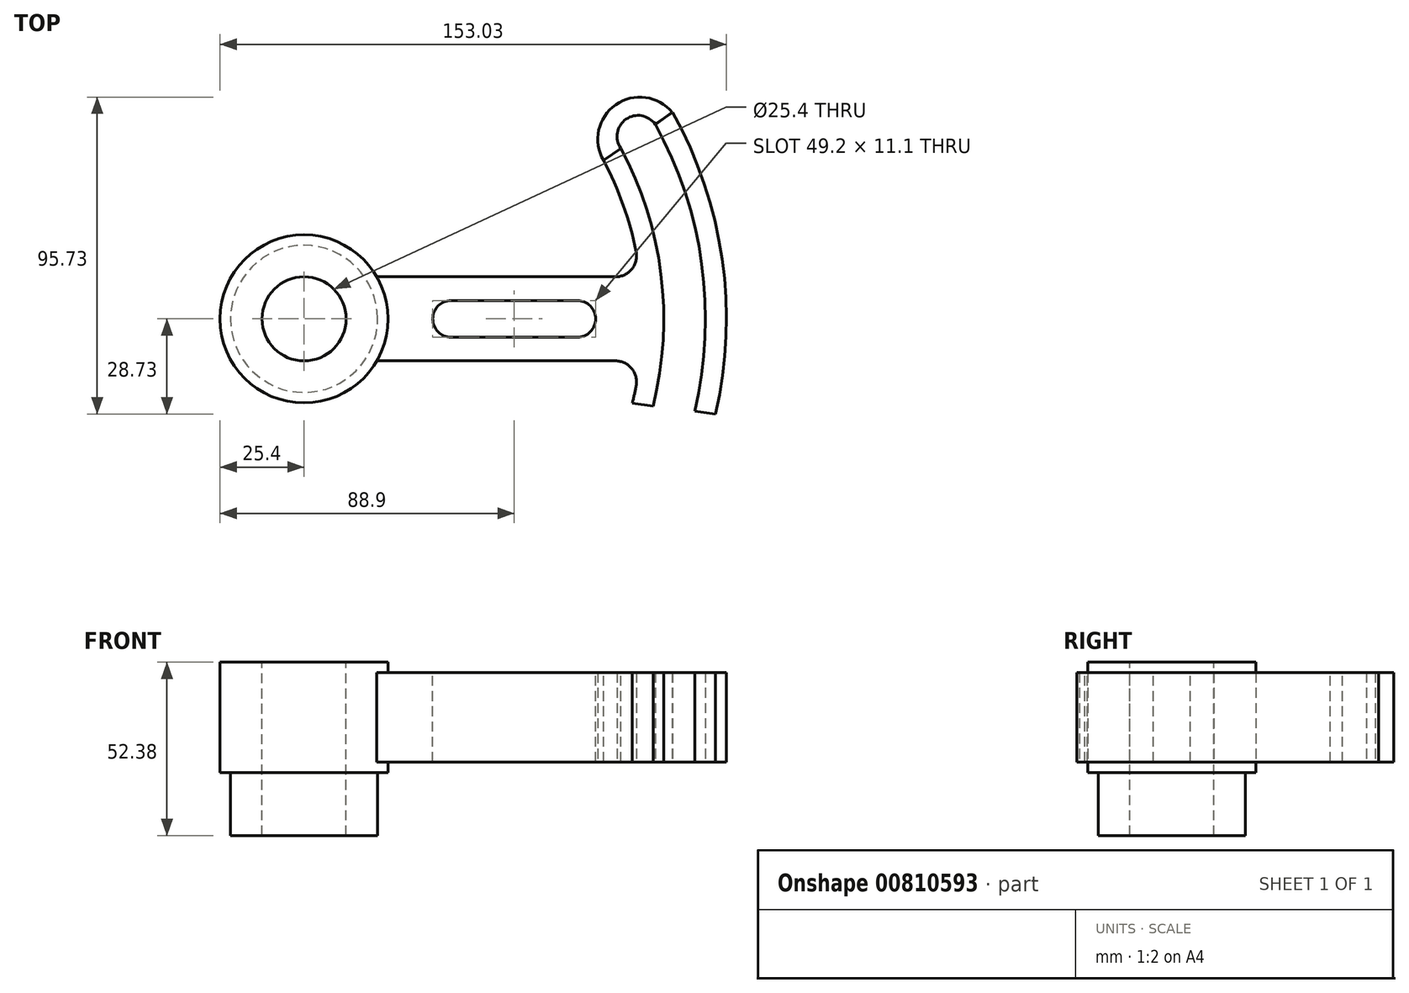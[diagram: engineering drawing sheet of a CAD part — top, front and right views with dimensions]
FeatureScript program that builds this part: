
annotation { "Feature Type Name" : "Feature", "Feature Type Description" : "" }
export const myFeature = defineFeature(function(context is Context, id is Id, definition is map)
    precondition{}
    {
        {
            var Q0;
            Q0=qCreatedBy(makeId("Top.planeOp"),FACE);
            var sketch = newSketch(context, id + "F0", { "sketchPlane" : qUnion([Q0])});
            skCircle(sketch, "E0", {"center": v(0, 0) * mm, "radius": 25.4 * mm});
            skLineSegment(sketch, "E1", {"start": v(22, 12.7) * mm, "end": v(114.45, 12.7) * mm});
            skLineSegment(sketch, "E2", {"start": v(22, -12.7) * mm, "end": v(114.45, -12.7) * mm});
            skLineSegment(sketch, "E3", {"start": v(114.45, 12.7) * mm, "end": v(114.45, -12.7) * mm});
            skSolve(sketch);
        }
        {
            var Q0;
            {var subQ0=sQuery(id+"F0.wireOp",EDGE,"E1");Q0=makeQuery(id+"F0.imprint","IMPRINT",FACE,{"disambiguationData":[TD([[makeQuery(id+"F0.imprint","IMPRINT",EDGE,{"derivedFrom":subQ0}),-1.0]])]});}
            extrude(context, id + "F1", {"entities" : qUnion([Q0]), "depth" : 26.97 * mm, "offsetDistance" : 25.4 * mm});
        }
        {
            var Q0;
            Q0=makeQuery(id+"F1.opExtrude","CAP_FACE",FACE,{"disambiguationData":[OSD([sQuery(id+"F0.wireOp",EDGE,"E0"),sQuery(id+"F0.wireOp",EDGE,"E1"),sQuery(id+"F0.wireOp",EDGE,"E2"),sQuery(id+"F0.wireOp",EDGE,"E3")])],"isStart":false});
            var sketch = newSketch(context, id + "F2", { "sketchPlane" : qUnion([Q0])});
            skLineSegment(sketch, "E4.bottom", {"start": v(44.45, 5.55) * mm, "end": v(82.55, 5.55) * mm});
            skLineSegment(sketch, "E4.top", {"start": v(44.45, -5.55) * mm, "end": v(82.55, -5.55) * mm});
            skLineSegment(sketch, "E4.left", {"start": v(44.45, 5.55) * mm, "end": v(44.45, -5.55) * mm});
            skLineSegment(sketch, "E4.right", {"start": v(82.55, 5.55) * mm, "end": v(82.55, -5.55) * mm});
            skSolve(sketch);
        }
        {
            var Q0;
            Q0=makeQuery(id+"F2.imprint","IMPRINT",FACE,{"disambiguationData":[TD([[makeQuery(id+"F2.imprint","IMPRINT",EDGE,{"derivedFrom":sQuery(id+"F2.wireOp",EDGE,"E4.bottom")}),1.0]])]});
            var sketch = newSketch(context, id + "F3", { "sketchPlane" : qUnion([Q0])});
            skCircle(sketch, "E5", {"center": v(44.45, 0) * mm, "radius": 5.55 * mm});
            skSolve(sketch);
        }
        {
            var Q0;
            Q0=makeQuery(id+"F2.imprint","IMPRINT",FACE,{"disambiguationData":[TD([[makeQuery(id+"F2.imprint","IMPRINT",EDGE,{"derivedFrom":sQuery(id+"F2.wireOp",EDGE,"E4.bottom")}),1.0]])]});
            var sketch = newSketch(context, id + "F4", { "sketchPlane" : qUnion([Q0])});
            skCircle(sketch, "E6", {"center": v(82.55, 0) * mm, "radius": 5.55 * mm});
            skSolve(sketch);
        }
        {
            var Q0;
            {var subQ1=makeQuery(id+"F2.imprint","IMPRINT",EDGE,{"derivedFrom":sQuery(id+"F2.wireOp",EDGE,"E4.right")});Q0=makeQuery(id+"F4.imprint","IMPRINT",FACE,{"disambiguationData":[TD([[makeQuery(id+"F4.imprint","IMPRINT",EDGE,{"derivedFrom":subQ1}),1.0]])]});}
            var Q1;
            Q1=makeQuery(id+"F2.imprint","IMPRINT",FACE,{"disambiguationData":[TD([[makeQuery(id+"F2.imprint","IMPRINT",EDGE,{"derivedFrom":sQuery(id+"F2.wireOp",EDGE,"E4.bottom")}),-1.0]])]});
            var Q2;
            {var subQ1=makeQuery(id+"F2.imprint","IMPRINT",EDGE,{"derivedFrom":sQuery(id+"F2.wireOp",EDGE,"E4.left")});Q2=makeQuery(id+"F3.imprint","IMPRINT",FACE,{"disambiguationData":[TD([[makeQuery(id+"F3.imprint","IMPRINT",EDGE,{"derivedFrom":subQ1}),-1.0]])]});}
            extrude(context, id + "F5", {"entities" : qUnion([Q0, Q1, Q2]), "operationType" : NewBodyOperationType.REMOVE, "oppositeDirection" : true, "depth" : 38.1 * mm, "offsetDistance" : 25.4 * mm});
        }
        {
            var Q0;
            Q0=qCreatedBy(makeId("Top.planeOp"),FACE);
            var sketch = newSketch(context, id + "F6", { "sketchPlane" : qUnion([Q0])});
            skCircle(sketch, "E7", {"center": v(0, 0) * mm, "radius": 25.4 * mm});
            skSolve(sketch);
        }
        {
            var Q0;
            Q0=makeQuery(id+"F6.imprint","IMPRINT",FACE,{"disambiguationData":[TD([[makeQuery(id+"F6.imprint","IMPRINT",EDGE,{"derivedFrom":sQuery(id+"F6.wireOp",EDGE,"E7")}),1.0]])]});
            extrude(context, id + "F7", {"entities" : qUnion([Q0]), "operationType" : NewBodyOperationType.ADD, "depth" : 30.15 * mm, "offsetDistance" : 25.4 * mm});
        }
        {
            var Q0;
            Q0=makeQuery(id+"F7.boolean.opBoolean","MERGE",FACE,{"derivedFrom":[makeQuery(id+"F1.opExtrude","CAP_FACE",FACE,{"disambiguationData":[OSD([sQuery(id+"F0.wireOp",EDGE,"E0"),sQuery(id+"F0.wireOp",EDGE,"E1"),sQuery(id+"F0.wireOp",EDGE,"E2"),sQuery(id+"F0.wireOp",EDGE,"E3")])],"isStart":true}),makeQuery(id+"F7.opExtrude","CAP_FACE",FACE,{"disambiguationData":[OSD([sQuery(id+"F6.wireOp",EDGE,"E7")])],"isStart":true})]});
            var sketch = newSketch(context, id + "F8", { "sketchPlane" : qUnion([Q0])});
            skCircle(sketch, "E8", {"center": v(0, 0) * mm, "radius": 25.4 * mm});
            skSolve(sketch);
        }
        {
            var Q0;
            Q0 = qSketchRegion(id + "F8", true);
            extrude(context, id + "F9", {"entities" : qUnion([Q0]), "operationType" : NewBodyOperationType.ADD, "depth" : 3.17 * mm, "offsetDistance" : 25.4 * mm});
        }
        {
            var Q0;
            Q0=makeQuery(id+"F9.opExtrude","CAP_FACE",FACE,{"disambiguationData":[OSD([sQuery(id+"F8.wireOp",EDGE,"E8")])],"isStart":false});
            var sketch = newSketch(context, id + "F10", { "sketchPlane" : qUnion([Q0])});
            skCircle(sketch, "E9", {"center": v(0, 0) * mm, "radius": 22.23 * mm});
            skSolve(sketch);
        }
        {
            var Q0;
            Q0=makeQuery(id+"F10.imprint","IMPRINT",FACE,{"disambiguationData":[TD([[makeQuery(id+"F10.imprint","IMPRINT",EDGE,{"derivedFrom":sQuery(id+"F10.wireOp",EDGE,"E9")}),1.0]])]});
            extrude(context, id + "F11", {"entities" : qUnion([Q0]), "operationType" : NewBodyOperationType.ADD, "depth" : 19.05 * mm, "offsetDistance" : 25.4 * mm});
        }
        {
            var Q0;
            Q0=makeQuery(id+"F7.opExtrude","CAP_FACE",FACE,{"disambiguationData":[OSD([sQuery(id+"F6.wireOp",EDGE,"E7")])],"isStart":false});
            var sketch = newSketch(context, id + "F12", { "sketchPlane" : qUnion([Q0])});
            skCircle(sketch, "E10", {"center": v(0, 0) * mm, "radius": 12.7 * mm});
            skSolve(sketch);
        }
        {
            var Q0;
            Q0=makeQuery(id+"F12.imprint","IMPRINT",FACE,{"disambiguationData":[TD([[makeQuery(id+"F12.imprint","IMPRINT",EDGE,{"derivedFrom":sQuery(id+"F12.wireOp",EDGE,"E10")}),1.0]])]});
            extrude(context, id + "F13", {"entities" : qUnion([Q0]), "operationType" : NewBodyOperationType.REMOVE, "oppositeDirection" : true, "depth" : 61.98 * mm, "offsetDistance" : 25.4 * mm});
        }
        {
            var Q0;
            Q0=makeQuery(id+"F1.opExtrude","SWEPT_FACE",FACE,{"disambiguationData":[OSD([sQuery(id+"F0.wireOp",EDGE,"E2")])]});
            var sketch = newSketch(context, id + "F14", { "sketchPlane" : qUnion([Q0])});
            skLineSegment(sketch, "E11.bottom", {"start": v(101.6, 0) * mm, "end": v(107.95, 0) * mm});
            skLineSegment(sketch, "E11.top", {"start": v(101.6, 26.97) * mm, "end": v(107.95, 26.97) * mm});
            skLineSegment(sketch, "E11.left", {"start": v(101.6, 0) * mm, "end": v(101.6, 26.97) * mm});
            skLineSegment(sketch, "E11.right", {"start": v(107.95, 0) * mm, "end": v(107.95, 26.97) * mm});
            skLineSegment(sketch, "E12.bottom", {"start": v(120.65, 26.97) * mm, "end": v(127, 26.97) * mm});
            skLineSegment(sketch, "E12.top", {"start": v(120.65, 0) * mm, "end": v(127, 0) * mm});
            skLineSegment(sketch, "E12.left", {"start": v(120.65, 26.97) * mm, "end": v(120.65, 0) * mm});
            skLineSegment(sketch, "E12.right", {"start": v(127, 26.97) * mm, "end": v(127, 0) * mm});
            skSolve(sketch);
        }
        {
            var Q0;
            Q0=qCreatedBy(makeId("Right.planeOp"),FACE);
            var sketch = newSketch(context, id + "F15", { "sketchPlane" : qUnion([Q0])});
            skLineSegment(sketch, "E13", {"start": v(0, 0) * mm, "end": v(0, 69.13) * mm});
            skSolve(sketch);
        }
        {
            var Q0;
            Q0=makeQuery(id+"F1.opExtrude","SWEPT_FACE",FACE,{"disambiguationData":[OSD([sQuery(id+"F0.wireOp",EDGE,"E3")])]});
            extrude(context, id + "F16", {"entities" : qUnion([Q0]), "operationType" : NewBodyOperationType.REMOVE, "oppositeDirection" : true, "depth" : 7.62 * mm, "offsetDistance" : 25.4 * mm});
        }
        {
            var Q0;
            Q0=makeQuery(id+"F14.imprint","IMPRINT",FACE,{"disambiguationData":[TD([[makeQuery(id+"F14.imprint","IMPRINT",EDGE,{"derivedFrom":sQuery(id+"F14.wireOp",EDGE,"E11.bottom")}),1.0]])]});
            var Q1;
            Q1=makeQuery(id+"F14.imprint","IMPRINT",FACE,{"disambiguationData":[TD([[makeQuery(id+"F14.imprint","IMPRINT",EDGE,{"derivedFrom":sQuery(id+"F14.wireOp",EDGE,"E12.bottom")}),-1.0]])]});
            var Q2;
            Q2=sQuery(id+"F15.wireOp",EDGE,"E13");
            revolve(context, id + "F17", {"operationType" : NewBodyOperationType.ADD, "surfaceOperationType" : NewSurfaceOperationType.NEW, "entities" : qUnion([Q0, Q1]), "axis" : qUnion([Q2]), "revolveType" : RevolveType.TWO_DIRECTIONS, "angle" : 35 * degree, "angleBack" : 352.7 * degree});
        }
        {
            var Q0;
            Q0=makeQuery(id+"F17.boolean.opBoolean","MERGE",FACE,{"derivedFrom":[makeQuery(id+"F7.boolean.opBoolean","MERGE",FACE,{"derivedFrom":[makeQuery(id+"F1.opExtrude","CAP_FACE",FACE,{"disambiguationData":[OSD([sQuery(id+"F0.wireOp",EDGE,"E0"),sQuery(id+"F0.wireOp",EDGE,"E1"),sQuery(id+"F0.wireOp",EDGE,"E2"),sQuery(id+"F0.wireOp",EDGE,"E3")])],"isStart":true}),makeQuery(id+"F7.opExtrude","CAP_FACE",FACE,{"disambiguationData":[OSD([sQuery(id+"F6.wireOp",EDGE,"E7")])],"isStart":true})]}),makeQuery(id+"F17.opRevolve","SWEPT_FACE",FACE,{"disambiguationData":[OSD([sQuery(id+"F14.wireOp",EDGE,"E11.bottom")])]})]});
            var sketch = newSketch(context, id + "F18", { "sketchPlane" : qUnion([Q0])});
            skArc(sketch, "E14", {"start": v(90.51, -47.87) * mm, "mid": v(94.2, -64.7) * mm, "end": v(111.27, -62.37) * mm});
            skArc(sketch, "E15", {"start": v(95.71, -51.51) * mm, "mid": v(97.3, -60.33) * mm, "end": v(106.13, -58.78) * mm});
            skLineSegment(sketch, "E16", {"start": v(90.51, -47.87) * mm, "end": v(95.71, -51.51) * mm});
            skLineSegment(sketch, "E17", {"start": v(106.13, -58.78) * mm, "end": v(111.27, -62.37) * mm});
            skSolve(sketch);
        }
        {
            var Q0;
            Q0=makeQuery(id+"F18.imprint","IMPRINT",FACE,{"disambiguationData":[TD([[makeQuery(id+"F18.imprint","IMPRINT",EDGE,{"derivedFrom":makeQuery(id+"F9.opExtrude","CAP_EDGE",EDGE,{"disambiguationData":[OSD([sQuery(id+"F8.wireOp",EDGE,"E8")])],"isStart":true})}),-1.0]])]});
            var sketch = newSketch(context, id + "F19", { "sketchPlane" : qUnion([Q0])});
            skArc(sketch, "E18", {"start": v(124.36, 28.72) * mm, "mid": v(110.13, 39.9) * mm, "end": v(99.16, 25.5) * mm});
            skArc(sketch, "E19", {"start": v(118.09, 27.92) * mm, "mid": v(110.93, 33.8) * mm, "end": v(105.52, 26.27) * mm});
            skLineSegment(sketch, "E20", {"start": v(99.16, 25.5) * mm, "end": v(105.52, 26.27) * mm});
            skLineSegment(sketch, "E21", {"start": v(118.09, 27.92) * mm, "end": v(124.36, 28.72) * mm});
            skSolve(sketch);
        }
        {
            var Q0;
            Q0=makeQuery(id+"F18.imprint","IMPRINT",FACE,{"disambiguationData":[TD([[makeQuery(id+"F18.imprint","IMPRINT",EDGE,{"derivedFrom":sQuery(id+"F18.wireOp",EDGE,"E14")}),1.0]])]});
            var Q1;
            {var subQ7=sQuery(id+"F19.wireOp",EDGE,"E18");Q1=makeQuery(id+"F19.imprint","IMPRINT",FACE,{"disambiguationData":[TD([[makeQuery(id+"F19.imprint","IMPRINT",EDGE,{"derivedFrom":subQ7}),1.0]])]});}
            extrude(context, id + "F20", {"entities" : qUnion([Q0, Q1]), "oppositeDirection" : true, "depth" : 26.97 * mm, "offsetDistance" : 25.4 * mm});
        }
        {
            var Q0;
            Q0=makeQuery(id+"F1.opExtrude","SWEPT_EDGE",EDGE,{"disambiguationData":[OSD([sQuery(id+"F0.wireOp",EDGE,"E0"),sQuery(id+"F0.wireOp",EDGE,"E1")])]});
            var Q1;
            Q1=makeQuery(id+"F1.opExtrude","SWEPT_EDGE",EDGE,{"disambiguationData":[OSD([sQuery(id+"F0.wireOp",EDGE,"E0"),sQuery(id+"F0.wireOp",EDGE,"E2")])]});
            var Q2;
            Q2=makeQuery(id+"F17.boolean.opBoolean","INTERSECT",EDGE,{"derivedFrom":[makeQuery(id+"F1.opExtrude","SWEPT_FACE",FACE,{"disambiguationData":[OSD([sQuery(id+"F0.wireOp",EDGE,"E1")])]}),makeQuery(id+"F17.opRevolve","SWEPT_FACE",FACE,{"disambiguationData":[OSD([sQuery(id+"F14.wireOp",EDGE,"E11.left")])]})]});
            var Q3;
            Q3=makeQuery(id+"F17.boolean.opBoolean","INTERSECT",EDGE,{"derivedFrom":[makeQuery(id+"F1.opExtrude","SWEPT_FACE",FACE,{"disambiguationData":[OSD([sQuery(id+"F0.wireOp",EDGE,"E2")])]}),makeQuery(id+"F17.opRevolve","SWEPT_FACE",FACE,{"disambiguationData":[OSD([sQuery(id+"F14.wireOp",EDGE,"E11.left")])]})]});
            fillet(context, id + "F21", {"entities" : qUnion([Q0, Q1, Q2, Q3]), "radius" : 6.35 * mm, "tangentPropagation" : true, "allowEdgeOverflow" : false});
        }
    });
